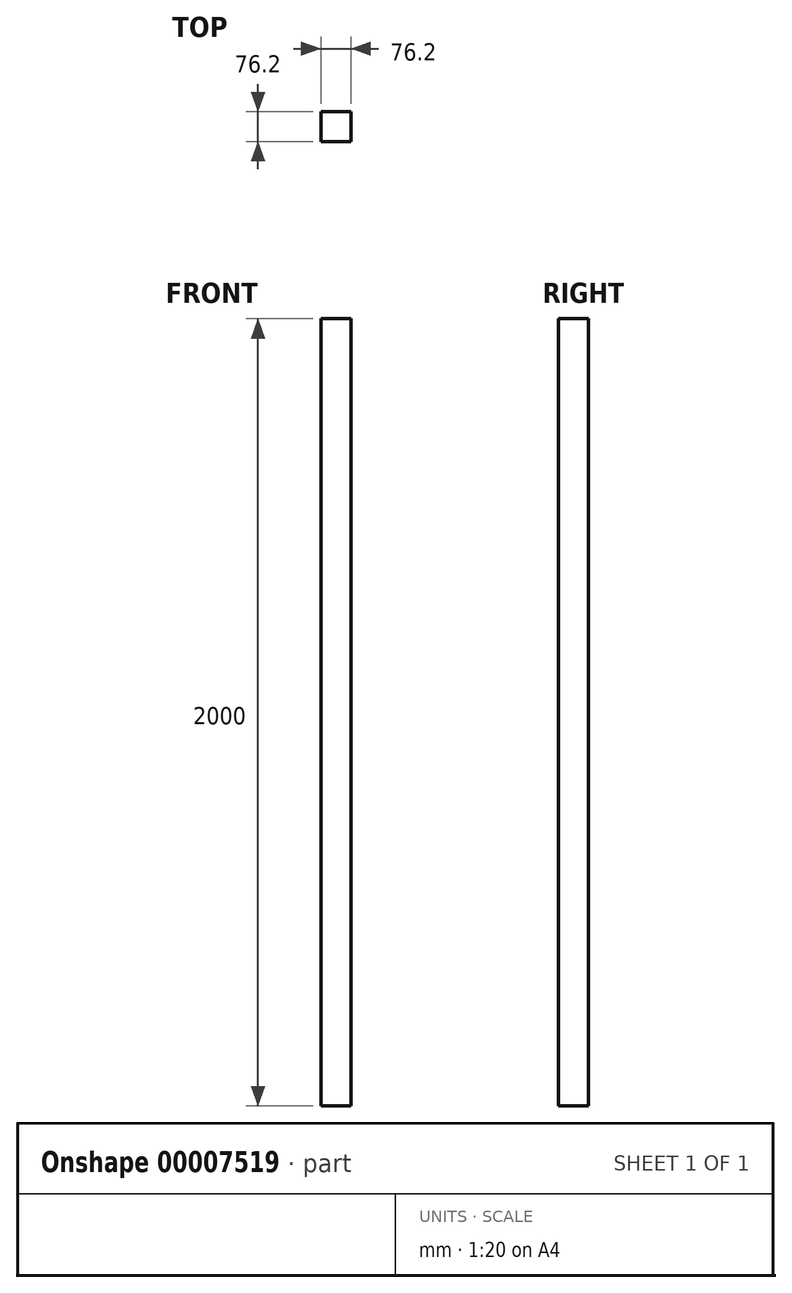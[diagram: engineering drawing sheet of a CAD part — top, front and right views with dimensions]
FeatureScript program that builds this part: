
annotation { "Feature Type Name" : "Feature", "Feature Type Description" : "" }
export const myFeature = defineFeature(function(context is Context, id is Id, definition is map)
    precondition{}
    {
        {
            var Q0;
            Q0=qCreatedBy(makeId("Top.planeOp"),FACE);
            var sketch = newSketch(context, id + "F0", { "sketchPlane" : qUnion([Q0])});
            skLineSegment(sketch, "E0", {"start": v(0, 38.1) * mm, "end": v(0, -38.1) * mm, "construction": true});
            skLineSegment(sketch, "E1", {"start": v(-38.1, 0) * mm, "end": v(38.1, 0) * mm, "construction": true});
            skLineSegment(sketch, "E2.bottom", {"start": v(-38.1, 38.1) * mm, "end": v(38.1, 38.1) * mm});
            skLineSegment(sketch, "E2.top", {"start": v(-38.1, -38.1) * mm, "end": v(38.1, -38.1) * mm});
            skLineSegment(sketch, "E2.left", {"start": v(-38.1, 38.1) * mm, "end": v(-38.1, -38.1) * mm});
            skLineSegment(sketch, "E2.right", {"start": v(38.1, 38.1) * mm, "end": v(38.1, -38.1) * mm});
            skSolve(sketch);
        }
        {
            var Q0;
            Q0=makeQuery(id+"F0.imprint","IMPRINT",FACE,{"disambiguationData":[TD([[makeQuery(id+"F0.imprint","IMPRINT",EDGE,{"derivedFrom":sQuery(id+"F0.wireOp",EDGE,"E2.bottom")}),-1.0]])]});
            extrude(context, id + "F1", {"entities" : qUnion([Q0]), "depth" : 2000 * mm, "symmetric" : true});
        }
    });
